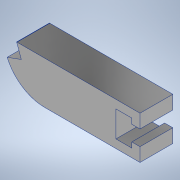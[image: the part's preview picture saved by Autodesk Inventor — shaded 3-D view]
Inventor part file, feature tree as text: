
AUTODESK INVENTOR PART (.ipt)
format: ipt  version: 2022 (Build 260153000, 153)  size: 157,696 bytes
history: native  units: mm
features: extrude x3, sketch x3, fillet x1
ambient origin geometry x8: Origin, YZ Plane, XZ Plane, XY Plane, X Axis, Y Axis, Z Axis, Center Point
bodies: Body1 (feature_tree)
feature tree (7):
  extrude  "Extrusion2"  Depth=5.8mm
  extrude  "Extrusion6"  Depth=12.0mm
  extrude  "Extrusion8"  TaperAngle=0.0deg  [1 undecoded]
  fillet  "Fillet2"  Radius=36.2mm
  sketch  "Sketch5"  dims[d41=5.8mm d48=44.0mm]
  sketch  "Sketch9"  dims[d56=12.0mm d57=0.0mm d63=45.0mm]
  sketch  "Sketch11"  dims[d67=15.6mm d71=0.0mm d72=36.2mm d85=5.6mm d86=9.5mm d87=3.0mm d89=5.0mm d90=0.0mm d91=0.0mm d92=19.198622mm d93=10.0mm d98=5.5mm d99=0.0mm d100=0.0mm d101=15.0mm]
note: 1 required parameter value undecoded (feature->parameter linkage not recoverable at this tier; creation-order binding heuristic only, values carry confidence <= 0.55)
